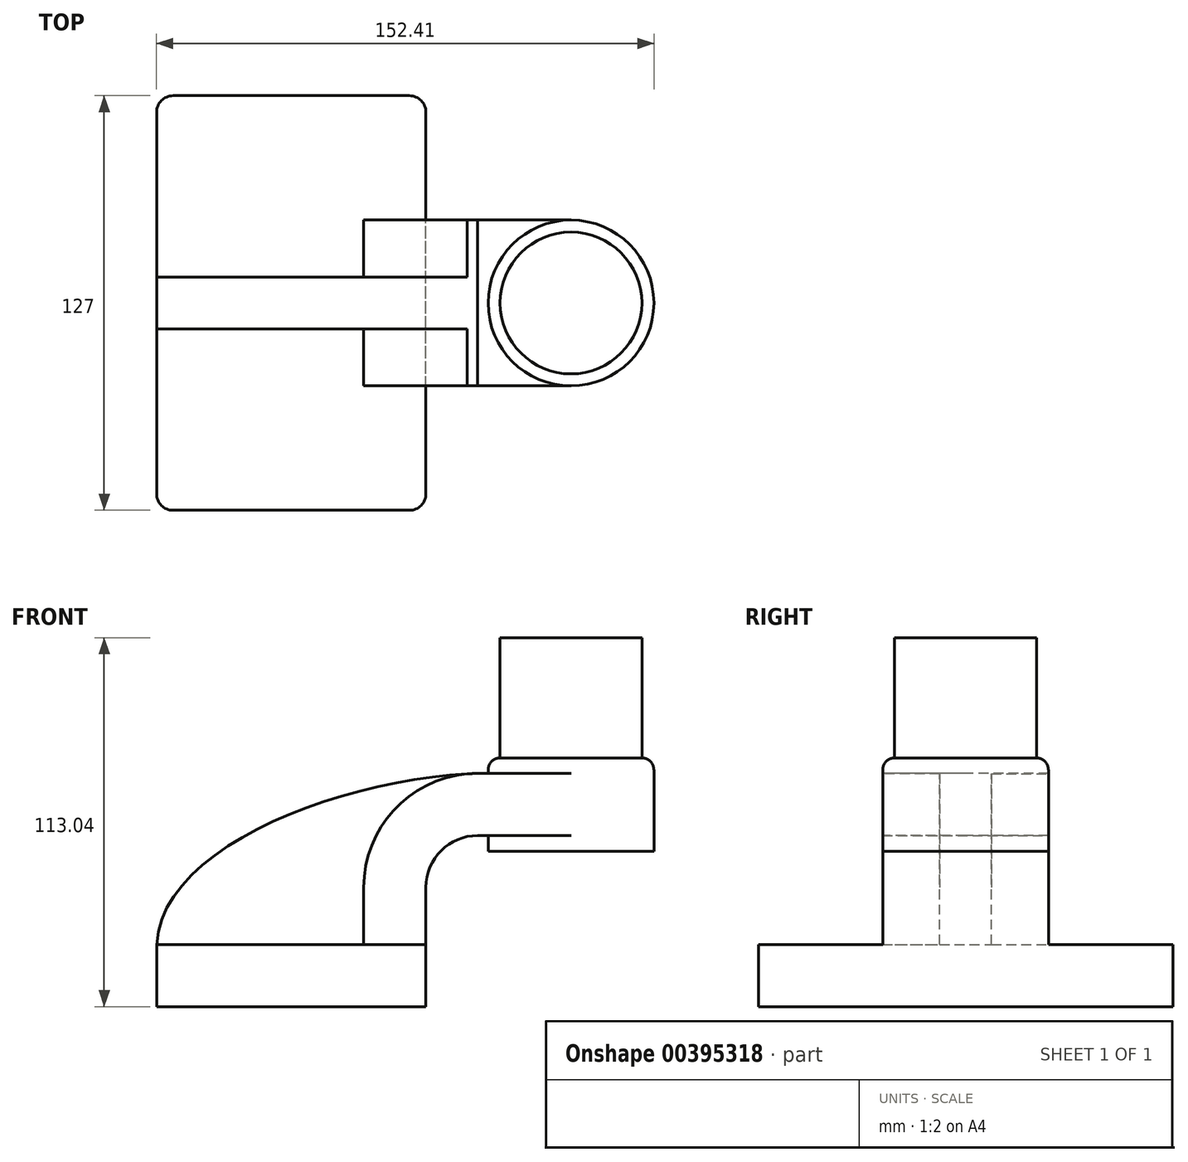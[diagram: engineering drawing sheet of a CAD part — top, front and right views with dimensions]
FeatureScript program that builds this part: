
annotation { "Feature Type Name" : "Feature", "Feature Type Description" : "" }
export const myFeature = defineFeature(function(context is Context, id is Id, definition is map)
    precondition{}
    {
        {
            var Q0;
            Q0=qCreatedBy(makeId("Front.planeOp"),FACE);
            var sketch = newSketch(context, id + "F0", { "sketchPlane" : qUnion([Q0])});
            skLineSegment(sketch, "E0.rect.bottom", {"start": v(-41.28, 9.52) * mm, "end": v(41.28, 9.52) * mm});
            skLineSegment(sketch, "E0.rect.top", {"start": v(-41.28, -9.52) * mm, "end": v(41.28, -9.52) * mm});
            skLineSegment(sketch, "E0.rect.left", {"start": v(-41.28, 9.52) * mm, "end": v(-41.28, -9.52) * mm});
            skLineSegment(sketch, "E0.rect.right", {"start": v(41.28, 9.52) * mm, "end": v(41.28, -9.52) * mm});
            skPoint(sketch, "E0.rect.middle", {"position": v(0, 0) * mm});
            skLineSegment(sketch, "E1", {"start": v(41.28, 9.52) * mm, "end": v(41.28, 27) * mm});
            skArc(sketch, "E2", {"start": v(41.28, 27) * mm, "mid": v(45.92, 38.23) * mm, "end": v(57.15, 42.88) * mm});
            skLineSegment(sketch, "E3", {"start": v(57.15, 42.88) * mm, "end": v(85.72, 42.88) * mm});
            skLineSegment(sketch, "E4.rect.bottom", {"start": v(60.32, 38.1) * mm, "end": v(111.12, 38.1) * mm});
            skLineSegment(sketch, "E4.rect.top", {"start": v(60.32, 66.68) * mm, "end": v(111.12, 66.68) * mm});
            skLineSegment(sketch, "E4.rect.left", {"start": v(60.32, 38.1) * mm, "end": v(60.32, 66.68) * mm});
            skLineSegment(sketch, "E4.rect.right", {"start": v(111.13, 38.1) * mm, "end": v(111.12, 66.68) * mm});
            skPoint(sketch, "E4.rect.middle", {"position": v(85.72, 52.39) * mm});
            skLineSegment(sketch, "E5.0", {"start": v(57.15, 61.93) * mm, "end": v(85.72, 61.93) * mm});
            skArc(sketch, "E5.1", {"start": v(22.23, 27) * mm, "mid": v(32.45, 51.7) * mm, "end": v(57.15, 61.93) * mm});
            skLineSegment(sketch, "E5.2", {"start": v(22.23, 9.52) * mm, "end": v(22.23, 27) * mm});
            skLineSegment(sketch, "E6", {"start": v(85.72, 38.1) * mm, "end": v(85.72, 66.68) * mm});
            skFitSpline(sketch, "E7", {"points": [v(-41.28, 9.53) * mm, v(57.15, 61.93) * mm], "startDerivative": vector(5.2, 92.34) * mm, "endDerivative": vector(120.92, 4.22) * mm});
            skSolve(sketch);
        }
        {
            var Q0;
            Q0=makeQuery(id+"F0.imprint","IMPRINT",FACE,{"disambiguationData":[TD([[makeQuery(id+"F0.imprint","IMPRINT",EDGE,{"derivedFrom":sQuery(id+"F0.wireOp",EDGE,"E0.rect.top")}),1.0]])]});
            extrude(context, id + "F1", {"entities" : qUnion([Q0]), "endBound" : BoundingType.SYMMETRIC, "depth" : 127 * mm});
        }
        {
            var Q0;
            {var subQ9=sQuery(id+"F0.wireOp",EDGE,"E1");Q0=makeQuery(id+"F0.imprint","IMPRINT",FACE,{"disambiguationData":[TD([[makeQuery(id+"F0.imprint","IMPRINT",EDGE,{"derivedFrom":subQ9}),1.0]])]});}
            var Q1;
            {var subQ0=sQuery(id+"F0.wireOp",EDGE,"E6");var subQ1=sQuery(id+"F0.wireOp",EDGE,"E3");var subQ2=makeQuery(id+"F0.imprint","INTERSECT",VERTEX,{"derivedFrom":[subQ1,subQ0]});Q1=makeQuery(id+"F0.imprint","IMPRINT",FACE,{"disambiguationData":[TD([[makeQuery(id+"F0.imprint","IMPRINT",EDGE,{"disambiguationData":[TD([[subQ2,1.0]])],"derivedFrom":subQ1}),1.0]])]});}
            extrude(context, id + "F2", {"entities" : qUnion([Q0, Q1]), "operationType" : NewBodyOperationType.ADD, "endBound" : BoundingType.SYMMETRIC, "depth" : 50.8 * mm});
        }
        {
            var Q0;
            {var subQ3=sQuery(id+"F0.wireOp",EDGE,"E5.2");Q0=makeQuery(id+"F0.imprint","IMPRINT",FACE,{"disambiguationData":[TD([[makeQuery(id+"F0.imprint","IMPRINT",EDGE,{"derivedFrom":subQ3}),1.0]])]});}
            extrude(context, id + "F3", {"entities" : qUnion([Q0]), "operationType" : NewBodyOperationType.ADD, "endBound" : BoundingType.SYMMETRIC, "depth" : 15.88 * mm});
        }
        {
            var Q0;
            {var subQ5=sQuery(id+"F0.wireOp",EDGE,"E4.rect.right");Q0=makeQuery(id+"F0.imprint","IMPRINT",FACE,{"disambiguationData":[TD([[makeQuery(id+"F0.imprint","IMPRINT",EDGE,{"derivedFrom":subQ5}),1.0]])]});}
            var Q1;
            Q1=sQuery(id+"F0.wireOp",EDGE,"E6");
            revolve(context, id + "F4", {"operationType" : NewBodyOperationType.ADD, "entities" : qUnion([Q0]), "axis" : qUnion([Q1]), "revolveType" : RevolveType.FULL});
        }
        {
            var Q0;
            Q0=makeQuery(id+"F1.opExtrude","CAP_EDGE",EDGE,{"disambiguationData":[OSD([sQuery(id+"F0.wireOp",EDGE,"E0.rect.right")])],"isStart":false});
            var Q1;
            Q1=makeQuery(id+"F1.opExtrude","CAP_EDGE",EDGE,{"disambiguationData":[OSD([sQuery(id+"F0.wireOp",EDGE,"E0.rect.left")])],"isStart":false});
            var Q2;
            Q2=makeQuery(id+"F1.opExtrude","CAP_EDGE",EDGE,{"disambiguationData":[OSD([sQuery(id+"F0.wireOp",EDGE,"E0.rect.right")])],"isStart":true});
            var Q3;
            Q3=makeQuery(id+"F1.opExtrude","CAP_EDGE",EDGE,{"disambiguationData":[OSD([sQuery(id+"F0.wireOp",EDGE,"E0.rect.left")])],"isStart":true});
            fillet(context, id + "F5", {"entities" : qUnion([Q0, Q1, Q2, Q3]), "radius" : 5.08 * mm, "tangentPropagation" : true, "allowEdgeOverflow" : false});
        }
        {
            var Q0;
            Q0=makeQuery(id+"F4.opRevolve","SWEPT_EDGE",EDGE,{"disambiguationData":[OSD([sQuery(id+"F0.wireOp",EDGE,"E4.rect.top"),sQuery(id+"F0.wireOp",EDGE,"E4.rect.right")])]});
            fillet(context, id + "F6", {"entities" : qUnion([Q0]), "radius" : 3.68 * mm, "tangentPropagation" : true, "allowEdgeOverflow" : false});
        }
        {
            var Q0;
            Q0=makeQuery(id+"F4.opRevolve","SWEPT_FACE",FACE,{"disambiguationData":[OSD([sQuery(id+"F0.wireOp",EDGE,"E4.rect.top")])]});
            extrude(context, id + "F7", {"entities" : qUnion([Q0]), "operationType" : NewBodyOperationType.ADD, "depth" : 36.83 * mm});
        }
    });
